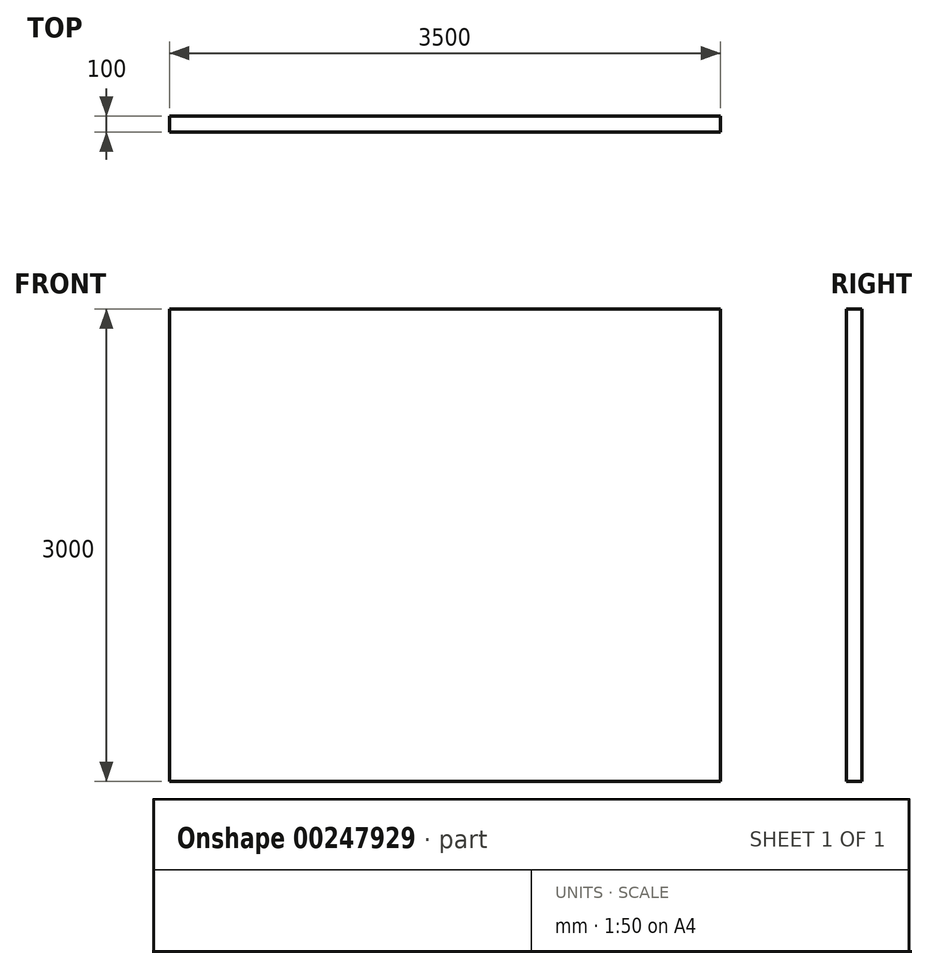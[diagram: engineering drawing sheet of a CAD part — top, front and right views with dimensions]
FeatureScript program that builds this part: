
annotation { "Feature Type Name" : "Feature", "Feature Type Description" : "" }
export const myFeature = defineFeature(function(context is Context, id is Id, definition is map)
    precondition{}
    {
        {
            var Q0;
            Q0=qCreatedBy(makeId("Front.planeOp"),FACE);
            var sketch = newSketch(context, id + "F0", { "sketchPlane" : qUnion([Q0])});
            skLineSegment(sketch, "E0.bottom", {"start": v(1750, 0) * mm, "end": v(-1750, 0) * mm});
            skLineSegment(sketch, "E0.top", {"start": v(1750, 3000) * mm, "end": v(-1750, 3000) * mm});
            skLineSegment(sketch, "E0.left", {"start": v(1750, 0) * mm, "end": v(1750, 3000) * mm});
            skLineSegment(sketch, "E0.right", {"start": v(-1750, 0) * mm, "end": v(-1750, 3000) * mm});
            skPoint(sketch, "E0.middle", {"position": v(0, 1500) * mm});
            skSolve(sketch);
        }
        {
            var Q0;
            Q0=makeQuery(id+"F0.imprint","IMPRINT",FACE,{"disambiguationData":[TD([[makeQuery(id+"F0.imprint","IMPRINT",EDGE,{"derivedFrom":sQuery(id+"F0.wireOp",EDGE,"E0.bottom")}),-1.0]])]});
            extrude(context, id + "F1", {"entities" : qUnion([Q0]), "endBound" : BoundingType.SYMMETRIC, "depth" : 100 * mm});
        }
    });
